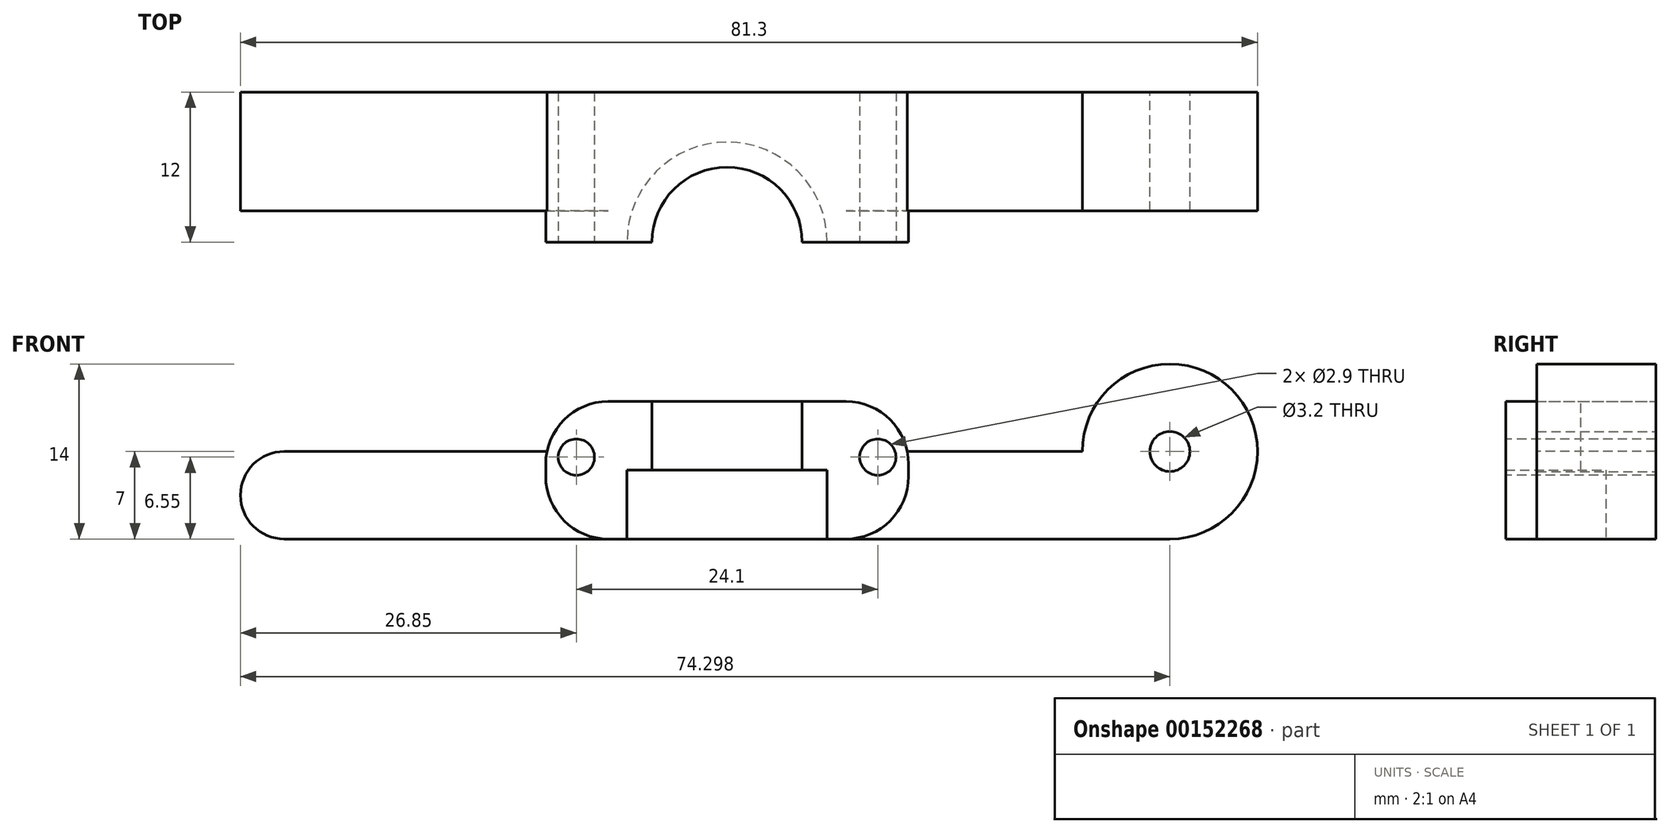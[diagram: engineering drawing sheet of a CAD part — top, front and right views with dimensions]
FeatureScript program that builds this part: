
annotation { "Feature Type Name" : "Feature", "Feature Type Description" : "" }
export const myFeature = defineFeature(function(context is Context, id is Id, definition is map)
    precondition{}
    {
        {
            var Q0;
            Q0=qCreatedBy(makeId("Front.planeOp"),FACE);
            var sketch = newSketch(context, id + "F0", { "sketchPlane" : qUnion([Q0])});
            skLineSegment(sketch, "E0.bottom", {"start": v(28.4, 3.5) * mm, "end": v(-35.4, 3.5) * mm});
            skLineSegment(sketch, "E0.top", {"start": v(35.4, -3.5) * mm, "end": v(-35.4, -3.5) * mm});
            skPoint(sketch, "E0.middle", {"position": v(0, 0) * mm});
            skArc(sketch, "E1", {"start": v(-35.4, 3.5) * mm, "mid": v(-38.9, 0) * mm, "end": v(-35.4, -3.5) * mm});
            skArc(sketch, "E2", {"start": v(35.4, -3.5) * mm, "mid": v(40.35, 8.45) * mm, "end": v(28.4, 3.5) * mm});
            skCircle(sketch, "E3", {"center": v(35.4, 3.5) * mm, "radius": 1.6 * mm});
            skSolve(sketch);
        }
        {
            var Q0;
            Q0=makeQuery(id+"F0.imprint","IMPRINT",FACE,{"disambiguationData":[TD([[makeQuery(id+"F0.imprint","IMPRINT",EDGE,{"derivedFrom":sQuery(id+"F0.wireOp",EDGE,"E0.bottom")}),1.0]])]});
            extrude(context, id + "F1", {"entities" : qUnion([Q0]), "endBound" : BoundingType.SYMMETRIC, "depth" : 9.5 * mm});
        }
        {
            var Q0;
            Q0=makeQuery(id+"F1.opExtrude","CAP_FACE",FACE,{"disambiguationData":[OSD([sQuery(id+"F0.wireOp",EDGE,"E0.bottom"),sQuery(id+"F0.wireOp",EDGE,"E0.top"),sQuery(id+"F0.wireOp",EDGE,"E1"),sQuery(id+"F0.wireOp",EDGE,"E2"),sQuery(id+"F0.wireOp",EDGE,"E3")])],"isStart":true});
            var sketch = newSketch(context, id + "F2", { "sketchPlane" : qUnion([Q0])});
            skLineSegment(sketch, "E4.bottom", {"start": v(-12.5, 7.5) * mm, "end": v(12.5, 7.5) * mm});
            skLineSegment(sketch, "E4.top", {"start": v(-12.5, -3.5) * mm, "end": v(12.5, -3.5) * mm});
            skLineSegment(sketch, "E4.left", {"start": v(-12.5, 7.5) * mm, "end": v(-12.5, -3.5) * mm});
            skLineSegment(sketch, "E4.right", {"start": v(12.5, 7.5) * mm, "end": v(12.5, -3.5) * mm});
            skSolve(sketch);
        }
        {
            var Q0;
            Q0 = qSketchRegion(id + "F2", true);
            extrude(context, id + "F3", {"entities" : qUnion([Q0]), "operationType" : NewBodyOperationType.ADD, "oppositeDirection" : true, "depth" : 12 * mm});
        }
        {
            var Q0;
            Q0=makeQuery(id+"F3.opExtrude","SWEPT_FACE",FACE,{"disambiguationData":[OSD([sQuery(id+"F2.wireOp",EDGE,"E4.bottom")])]});
            var sketch = newSketch(context, id + "F4", { "sketchPlane" : qUnion([Q0])});
            skCircle(sketch, "E5", {"center": v(0, -7.25) * mm, "radius": 6 * mm});
            skSolve(sketch);
        }
        {
            var Q0;
            {var subQ0=sQuery(id+"F4.wireOp",EDGE,"E5");var subQ1=makeQuery(id+"F3.opExtrude","CAP_EDGE",EDGE,{"disambiguationData":[OSD([sQuery(id+"F2.wireOp",EDGE,"E4.bottom")])],"isStart":false});var subQ2=makeQuery(id+"F4.imprint","INTERSECT",VERTEX,{"disambiguationData":[OD(0.0)],"derivedFrom":[subQ1,subQ0]});Q0=makeQuery(id+"F4.imprint","IMPRINT",FACE,{"disambiguationData":[TD([[makeQuery(id+"F4.imprint","IMPRINT",EDGE,{"disambiguationData":[TD([[subQ2,-1.0]])],"derivedFrom":subQ0}),1.0]])]});}
            var Q1;
            {var subQ0=sQuery(id+"F4.wireOp",EDGE,"E5");var subQ1=makeQuery(id+"F3.opExtrude","CAP_EDGE",EDGE,{"disambiguationData":[OSD([sQuery(id+"F2.wireOp",EDGE,"E4.bottom")])],"isStart":false});var subQ2=makeQuery(id+"F4.imprint","INTERSECT",VERTEX,{"disambiguationData":[OD(0.0)],"derivedFrom":[subQ1,subQ0]});Q1=makeQuery(id+"F4.imprint","IMPRINT",FACE,{"disambiguationData":[TD([[makeQuery(id+"F4.imprint","IMPRINT",EDGE,{"disambiguationData":[TD([[subQ2,1.0]])],"derivedFrom":subQ0}),1.0]])]});}
            extrude(context, id + "F5", {"entities" : qUnion([Q0, Q1]), "operationType" : NewBodyOperationType.REMOVE, "oppositeDirection" : true, "depth" : 6 * mm});
        }
        {
            var Q0;
            Q0=makeQuery(id+"F3.boolean.opBoolean","MERGE",FACE,{"derivedFrom":[makeQuery(id+"F1.opExtrude","SWEPT_FACE",FACE,{"disambiguationData":[OSD([sQuery(id+"F0.wireOp",EDGE,"E0.top")])]}),makeQuery(id+"F3.opExtrude","SWEPT_FACE",FACE,{"disambiguationData":[OSD([sQuery(id+"F2.wireOp",EDGE,"E4.top")])]})]});
            var sketch = newSketch(context, id + "F6", { "sketchPlane" : qUnion([Q0])});
            skCircle(sketch, "E6", {"center": v(0, 7.25) * mm, "radius": 8 * mm});
            skSolve(sketch);
        }
        {
            var Q0;
            {var subQ0=sQuery(id+"F6.wireOp",EDGE,"E6");var subQ1=makeQuery(id+"F3.opExtrude","CAP_EDGE",EDGE,{"disambiguationData":[OSD([sQuery(id+"F2.wireOp",EDGE,"E4.top")])],"isStart":false});var subQ2=makeQuery(id+"F6.imprint","INTERSECT",VERTEX,{"disambiguationData":[OD(0.0)],"derivedFrom":[subQ1,subQ0]});Q0=makeQuery(id+"F6.imprint","IMPRINT",FACE,{"disambiguationData":[TD([[makeQuery(id+"F6.imprint","IMPRINT",EDGE,{"disambiguationData":[TD([[subQ2,1.0]])],"derivedFrom":subQ0}),1.0]])]});}
            var Q1;
            {var subQ0=sQuery(id+"F6.wireOp",EDGE,"E6");var subQ1=makeQuery(id+"F3.opExtrude","CAP_EDGE",EDGE,{"disambiguationData":[OSD([sQuery(id+"F2.wireOp",EDGE,"E4.top")])],"isStart":false});var subQ2=makeQuery(id+"F6.imprint","INTERSECT",VERTEX,{"disambiguationData":[OD(0.0)],"derivedFrom":[subQ1,subQ0]});Q1=makeQuery(id+"F6.imprint","IMPRINT",FACE,{"disambiguationData":[TD([[makeQuery(id+"F6.imprint","IMPRINT",EDGE,{"disambiguationData":[TD([[subQ2,-1.0]])],"derivedFrom":subQ0}),1.0]])]});}
            var Q2;
            Q2=sQuery(id+"F6.wireOp",EDGE,"E6");
            extrude(context, id + "F7", {"entities" : qUnion([Q0, Q1]), "operationType" : NewBodyOperationType.REMOVE, "surfaceEntities" : qUnion([Q2]), "oppositeDirection" : true, "depth" : 5.5 * mm});
        }
        {
            var Q0;
            Q0=makeQuery(id+"F3.opExtrude","SWEPT_FACE",FACE,{"disambiguationData":[OSD([sQuery(id+"F2.wireOp",EDGE,"E4.left")])]});
            var sketch = newSketch(context, id + "F8", { "sketchPlane" : qUnion([Q0])});
            skLineSegment(sketch, "E7.bottom", {"start": v(-7.25, 7.5) * mm, "end": v(4.75, 7.5) * mm});
            skLineSegment(sketch, "E7.top", {"start": v(-7.25, -3.5) * mm, "end": v(4.75, -3.5) * mm});
            skLineSegment(sketch, "E7.left", {"start": v(4.75, 7.5) * mm, "end": v(4.75, -3.5) * mm});
            skLineSegment(sketch, "E7.right", {"start": v(-7.25, 7.5) * mm, "end": v(-7.25, -3.5) * mm});
            skSolve(sketch);
        }
        {
            var Q0;
            Q0 = qSketchRegion(id + "F8", true);
            extrude(context, id + "F9", {"entities" : qUnion([Q0]), "operationType" : NewBodyOperationType.ADD, "depth" : 2 * mm});
        }
        {
            var Q0;
            Q0=makeQuery(id+"F3.opExtrude","SWEPT_FACE",FACE,{"disambiguationData":[OSD([sQuery(id+"F2.wireOp",EDGE,"E4.right")])]});
            var sketch = newSketch(context, id + "F10", { "sketchPlane" : qUnion([Q0])});
            skLineSegment(sketch, "E8.bottom", {"start": v(7.25, 7.5) * mm, "end": v(-4.75, 7.5) * mm});
            skLineSegment(sketch, "E8.top", {"start": v(7.25, -3.5) * mm, "end": v(-4.75, -3.5) * mm});
            skLineSegment(sketch, "E8.left", {"start": v(-4.75, 7.5) * mm, "end": v(-4.75, -3.5) * mm});
            skLineSegment(sketch, "E8.right", {"start": v(7.25, 7.5) * mm, "end": v(7.25, -3.5) * mm});
            skSolve(sketch);
        }
        {
            var Q0;
            {var subQ1=sQuery(id+"F10.wireOp",EDGE,"E8.bottom");Q0=makeQuery(id+"F10.imprint","IMPRINT",FACE,{"disambiguationData":[TD([[makeQuery(id+"F10.imprint","IMPRINT",EDGE,{"derivedFrom":subQ1}),1.0]])]});}
            extrude(context, id + "F11", {"entities" : qUnion([Q0]), "operationType" : NewBodyOperationType.ADD, "depth" : 2 * mm});
        }
        {
            var Q0;
            {var subQ0=sQuery(id+"F2.wireOp",EDGE,"E4.right");var subQ1=sQuery(id+"F2.wireOp",EDGE,"E4.top");var subQ2=sQuery(id+"F2.wireOp",EDGE,"E4.bottom");Q0=makeQuery(id+"F11.boolean.opBoolean","MERGE",FACE,{"derivedFrom":[makeQuery(id+"F7.boolean.opBoolean","SPLIT",FACE,{"disambiguationData":[TD([makeQuery(id+"F3.opExtrude","SWEPT_FACE",FACE,{"disambiguationData":[OSD([subQ0])]})])],"derivedFrom":makeQuery(id+"F3.opExtrude","CAP_FACE",FACE,{"disambiguationData":[OSD([subQ2,subQ1,sQuery(id+"F2.wireOp",EDGE,"E4.left"),subQ0])],"isStart":false})}),makeQuery(id+"F11.opExtrude","SWEPT_FACE",FACE,{"disambiguationData":[OSD([sQuery(id+"F10.wireOp",EDGE,"E8.right")])]})]});}
            var sketch = newSketch(context, id + "F12", { "sketchPlane" : qUnion([Q0])});
            skCircle(sketch, "E9", {"center": v(-12.05, 3.05) * mm, "radius": 1.45 * mm});
            skSolve(sketch);
        }
        {
            var Q0;
            {var subQ0=sQuery(id+"F2.wireOp",EDGE,"E4.left");var subQ2=sQuery(id+"F2.wireOp",EDGE,"E4.top");var subQ3=sQuery(id+"F2.wireOp",EDGE,"E4.bottom");Q0=makeQuery(id+"F9.boolean.opBoolean","MERGE",FACE,{"derivedFrom":[makeQuery(id+"F7.boolean.opBoolean","SPLIT",FACE,{"disambiguationData":[TD([makeQuery(id+"F3.opExtrude","SWEPT_FACE",FACE,{"disambiguationData":[OSD([subQ0])]})])],"derivedFrom":makeQuery(id+"F3.opExtrude","CAP_FACE",FACE,{"disambiguationData":[OSD([subQ3,subQ2,subQ0,sQuery(id+"F2.wireOp",EDGE,"E4.right")])],"isStart":false})}),makeQuery(id+"F9.opExtrude","SWEPT_FACE",FACE,{"disambiguationData":[OSD([sQuery(id+"F8.wireOp",EDGE,"E7.right")])]})]});}
            var sketch = newSketch(context, id + "F13", { "sketchPlane" : qUnion([Q0])});
            skCircle(sketch, "E10", {"center": v(12.05, 3.05) * mm, "radius": 1.45 * mm});
            skSolve(sketch);
        }
        {
            var Q0;
            Q0=makeQuery(id+"F12.imprint","IMPRINT",FACE,{"disambiguationData":[TD([[makeQuery(id+"F12.imprint","IMPRINT",EDGE,{"derivedFrom":sQuery(id+"F12.wireOp",EDGE,"E9")}),1.0]])]});
            var Q1;
            Q1=sQuery(id+"F12.wireOp",EDGE,"E9");
            extrude(context, id + "F14", {"entities" : qUnion([Q0]), "operationType" : NewBodyOperationType.REMOVE, "surfaceEntities" : qUnion([Q1]), "oppositeDirection" : true, "depth" : 25 * mm});
        }
        {
            var Q0;
            Q0=makeQuery(id+"F13.imprint","IMPRINT",FACE,{"disambiguationData":[TD([[makeQuery(id+"F13.imprint","IMPRINT",EDGE,{"derivedFrom":sQuery(id+"F13.wireOp",EDGE,"E10")}),1.0]])]});
            extrude(context, id + "F15", {"entities" : qUnion([Q0]), "operationType" : NewBodyOperationType.REMOVE, "oppositeDirection" : true, "depth" : 25 * mm});
        }
        {
            var Q0;
            Q0=makeQuery(id+"F11.opExtrude","CAP_EDGE",EDGE,{"disambiguationData":[OSD([sQuery(id+"F10.wireOp",EDGE,"E8.top")])],"isStart":false});
            var Q1;
            Q1=makeQuery(id+"F11.opExtrude","CAP_EDGE",EDGE,{"disambiguationData":[OSD([sQuery(id+"F10.wireOp",EDGE,"E8.bottom")])],"isStart":false});
            var Q2;
            Q2=makeQuery(id+"F9.opExtrude","CAP_EDGE",EDGE,{"disambiguationData":[OSD([sQuery(id+"F8.wireOp",EDGE,"E7.top")])],"isStart":false});
            var Q3;
            Q3=makeQuery(id+"F9.opExtrude","CAP_EDGE",EDGE,{"disambiguationData":[OSD([sQuery(id+"F8.wireOp",EDGE,"E7.bottom")])],"isStart":false});
            fillet(context, id + "F16", {"entities" : qUnion([Q0, Q1, Q2, Q3]), "radius" : 5 * mm, "tangentPropagation" : true, "allowEdgeOverflow" : false});
        }
    });
